# Revit family: Chair-Soft_Seating-Allermuir-Conic-A632
name_source: partatom
category: Furniture
revit_build: Autodesk Revit MEP 2012 (Build: 20110309_2315)
units: mm (PartAtom-declared; Revit-internal decimal feet)

## types (1)
- A632
    04 CSI = 12 51 00
    2.5" Casters = No
    95 CSI = 12510
    A630 = No
    A631 = No
    A632 = Yes
    A633 = No
    A637 = No
    Advanced Sync Tilt with Multi Position Back = No
    Airflow Back Mesh = No
    Arm Height Range = 6.75" - 10.75"
    Assembly Code = E2020200
    Black Components = No
    Black GRP Base = No
    Black Gas Lift = No
    Black Plastic Back Membrane = No
    Brochure URL = http://www.allermuir.net
    CAD Blocks URL = http://www.allermuir.net
    Color Availability = See price list for material options
    Fabric Spec Sheets = http://www.allermuir.net
    Glide Finish = Plastic - Allermuir - White
    Height Adjustable Arms = No
    Height Adjustable Arms with Multi funtction Pad = No
    Height Range = 42" - 47.5"
    Leg Base = Plastic - Allermuir - White
    Leg Base 1 = Yes
    Lumbar Adjustment = No
    Manufacturer = Allermuir
    Manufacturer Fax = (419) 887 5805
    Model = A632
    Negative Seat Tilt = No
    Overall Depth = 600 mm
    Overall Height = 810 mm
    Overall Width = 730 mm  [stored 2.39501 ft]
    Plugin Data URL = http://products.ecoscorecard.com
    Polished Aluminum Arm Carrier = No
    Polished Aluminum Base = No
    Product Line = Conic
    Product Page URL = http://www.allermuir.net
    Seat Depth = 470 mm
    Seat Depth Adjustment = No
    Seat Height = 490 mm  [stored 1.60761 ft]
    Seat Height Range = 18.5" - 23.25"
    Seat or Base = Fabric - Allermuir - Silcoates
    Slimline Upholstery = No
    Specifications URL = http://www.allermuir.net
    Stacks = No
    Stand = Metal - Allermuir - Chrome - Polished
    Subcategory = Soft Seating
    Two Tone Upholstery = No
    URL = http://www.allermuir.net
    Weight = 37.00 lb
    White Plastic Back Membrane = No
    ecoScorecard Product Page = http://products.ecoscorecard.com
    ecoScorecard_data = http://thesenatorgroup.ecoscorecard.com

note: [stored X ft] marks values corroborated as IEEE doubles in the binary element streams (Revit-internal decimal feet)

## geometry (parser evidence)
native form markers: Blend x8, Sweep x3
no freeform markers — native parametric forms only
